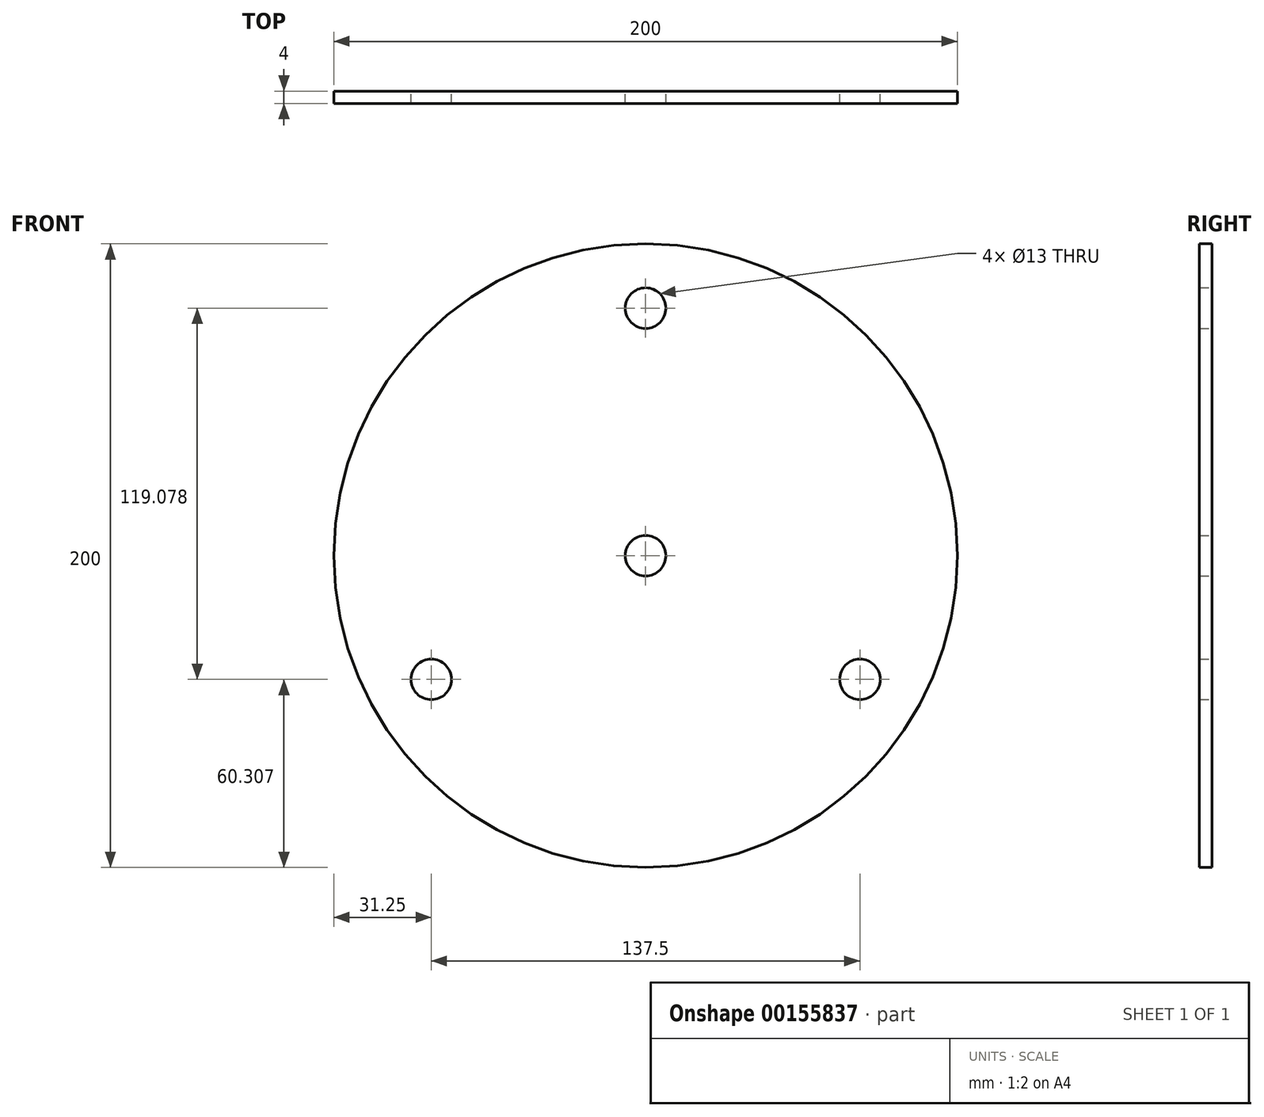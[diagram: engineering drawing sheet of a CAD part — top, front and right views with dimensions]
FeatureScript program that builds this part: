
annotation { "Feature Type Name" : "Feature", "Feature Type Description" : "" }
export const myFeature = defineFeature(function(context is Context, id is Id, definition is map)
    precondition{}
    {
        {
            var Q0;
            Q0=qCreatedBy(makeId("Front.planeOp"),FACE);
            var sketch = newSketch(context, id + "F0", { "sketchPlane" : qUnion([Q0])});
            skLineSegment(sketch, "E0", {"start": v(0, 0) * mm, "end": v(0, 79.39) * mm, "construction": true});
            skLineSegment(sketch, "E1", {"start": v(0, 79.39) * mm, "end": v(-68.75, -39.7) * mm, "construction": true});
            skLineSegment(sketch, "E2", {"start": v(-68.75, -39.7) * mm, "end": v(68.75, -39.7) * mm, "construction": true});
            skLineSegment(sketch, "E3", {"start": v(68.75, -39.7) * mm, "end": v(0, 79.39) * mm, "construction": true});
            skLineSegment(sketch, "E4", {"start": v(-68.75, -39.7) * mm, "end": v(0, 0) * mm, "construction": true});
            skLineSegment(sketch, "E5", {"start": v(68.75, -39.7) * mm, "end": v(0, 0) * mm, "construction": true});
            skCircle(sketch, "E6", {"center": v(0, 0) * mm, "radius": 79.39 * mm, "construction": true});
            skCircle(sketch, "E7", {"center": v(-68.75, -39.7) * mm, "radius": 6.5 * mm});
            skCircle(sketch, "E8", {"center": v(68.75, -39.7) * mm, "radius": 6.5 * mm});
            skCircle(sketch, "E9", {"center": v(0, 79.39) * mm, "radius": 6.5 * mm});
            skCircle(sketch, "E10", {"center": v(0, 0) * mm, "radius": 6.5 * mm});
            skCircle(sketch, "E11", {"center": v(0, 0) * mm, "radius": 100 * mm});
            skSolve(sketch);
        }
        {
            var Q0;
            Q0 = qSketchRegion(id + "F0", true);
            extrude(context, id + "F1", {"entities" : qUnion([Q0]), "depth" : 4 * mm});
        }
    });
